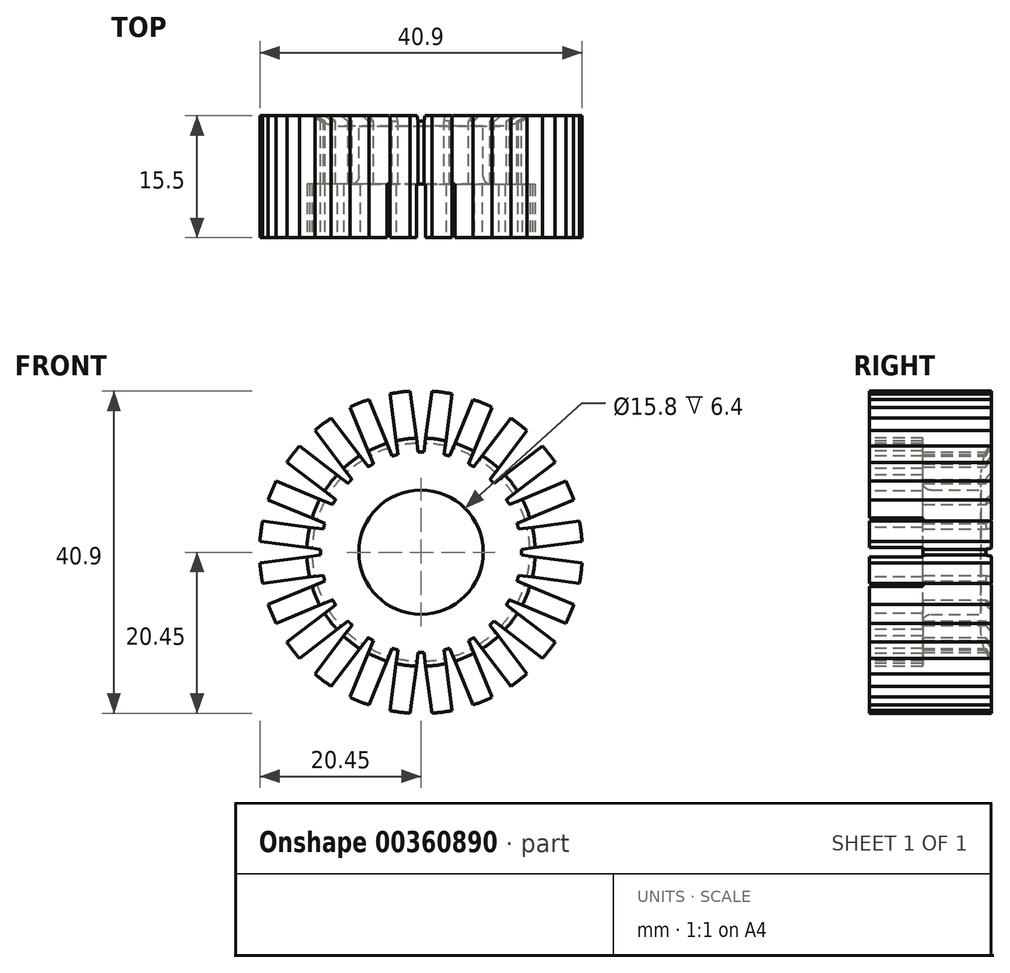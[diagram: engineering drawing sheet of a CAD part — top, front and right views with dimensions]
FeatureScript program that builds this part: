
annotation { "Feature Type Name" : "Feature", "Feature Type Description" : "" }
export const myFeature = defineFeature(function(context is Context, id is Id, definition is map)
    precondition{}
    {
        {
            var Q0;
            Q0=qCreatedBy(makeId("Front.planeOp"),FACE);
            var sketch = newSketch(context, id + "F0", { "sketchPlane" : qUnion([Q0])});
            skCircle(sketch, "E0", {"center": v(0, 0) * mm, "radius": 7.9 * mm});
            skCircle(sketch, "E1", {"center": v(0, 0) * mm, "radius": 12.75 * mm});
            skLineSegment(sketch, "E2", {"start": v(-29.1, 0) * mm, "end": v(30.08, 0) * mm, "construction": true});
            skLineSegment(sketch, "E3", {"start": v(4.61, 35.03) * mm, "end": v(-4.61, -35.03) * mm, "construction": true});
            skLineSegment(sketch, "E4", {"start": v(0.37, 12.74) * mm, "end": v(1.38, 20.45) * mm});
            skLineSegment(sketch, "E5", {"start": v(2.94, 12.4) * mm, "end": v(3.96, 20.11) * mm});
            skArc(sketch, "E6.trimOffspring", {"start": v(3.96, 20.11) * mm, "mid": v(2.68, 20.32) * mm, "end": v(1.38, 20.45) * mm});
            skLineSegment(sketch, "E7.1.0", {"start": v(6.05, 11.22) * mm, "end": v(9.03, 18.4) * mm});
            skArc(sketch, "E7.1.1", {"start": v(9.03, 18.4) * mm, "mid": v(7.85, 18.94) * mm, "end": v(6.63, 19.4) * mm});
            skLineSegment(sketch, "E7.1.2", {"start": v(3.65, 12.22) * mm, "end": v(6.63, 19.4) * mm});
            skLineSegment(sketch, "E7.2.0", {"start": v(8.75, 9.27) * mm, "end": v(13.49, 15.44) * mm});
            skArc(sketch, "E7.2.1", {"start": v(13.49, 15.44) * mm, "mid": v(12.48, 16.26) * mm, "end": v(11.42, 17.02) * mm});
            skLineSegment(sketch, "E7.2.2", {"start": v(6.69, 10.85) * mm, "end": v(11.42, 17.02) * mm});
            skLineSegment(sketch, "E7.3.0", {"start": v(10.85, 6.69) * mm, "end": v(17.02, 11.42) * mm});
            skArc(sketch, "E7.3.1", {"start": v(17.02, 11.42) * mm, "mid": v(16.26, 12.48) * mm, "end": v(15.44, 13.49) * mm});
            skLineSegment(sketch, "E7.3.2", {"start": v(9.27, 8.75) * mm, "end": v(15.44, 13.49) * mm});
            skLineSegment(sketch, "E7.4.0", {"start": v(12.22, 3.65) * mm, "end": v(19.4, 6.63) * mm});
            skArc(sketch, "E7.4.1", {"start": v(19.4, 6.63) * mm, "mid": v(18.94, 7.85) * mm, "end": v(18.4, 9.03) * mm});
            skLineSegment(sketch, "E7.4.2", {"start": v(11.22, 6.05) * mm, "end": v(18.4, 9.03) * mm});
            skLineSegment(sketch, "E7.5.0", {"start": v(12.74, 0.37) * mm, "end": v(20.45, 1.38) * mm});
            skArc(sketch, "E7.5.1", {"start": v(20.45, 1.38) * mm, "mid": v(20.32, 2.68) * mm, "end": v(20.11, 3.96) * mm});
            skLineSegment(sketch, "E7.5.2", {"start": v(12.4, 2.94) * mm, "end": v(20.11, 3.96) * mm});
            skLineSegment(sketch, "E7.6.0", {"start": v(12.4, -2.94) * mm, "end": v(20.11, -3.96) * mm});
            skArc(sketch, "E7.6.1", {"start": v(20.11, -3.96) * mm, "mid": v(20.32, -2.68) * mm, "end": v(20.45, -1.38) * mm});
            skLineSegment(sketch, "E7.6.2", {"start": v(12.74, -0.37) * mm, "end": v(20.45, -1.38) * mm});
            skLineSegment(sketch, "E7.7.0", {"start": v(11.22, -6.05) * mm, "end": v(18.4, -9.03) * mm});
            skArc(sketch, "E7.7.1", {"start": v(18.4, -9.03) * mm, "mid": v(18.94, -7.85) * mm, "end": v(19.4, -6.63) * mm});
            skLineSegment(sketch, "E7.7.2", {"start": v(12.22, -3.65) * mm, "end": v(19.4, -6.63) * mm});
            skLineSegment(sketch, "E7.anchor1", {"start": v(0, 0) * mm, "end": v(2.94, 12.4) * mm, "construction": true});
            skLineSegment(sketch, "E7.anchor2", {"start": v(0, 0) * mm, "end": v(-0.37, 12.74) * mm, "construction": true});
            skLineSegment(sketch, "E8.1.8.0", {"start": v(9.27, -8.75) * mm, "end": v(15.44, -13.49) * mm});
            skArc(sketch, "E8.3.8.0", {"start": v(15.44, -13.49) * mm, "mid": v(16.26, -12.48) * mm, "end": v(17.02, -11.42) * mm});
            skLineSegment(sketch, "E8.7.8.0", {"start": v(10.85, -6.69) * mm, "end": v(17.02, -11.42) * mm});
            skLineSegment(sketch, "E8.1.9.0", {"start": v(6.69, -10.85) * mm, "end": v(11.42, -17.02) * mm});
            skArc(sketch, "E8.3.9.0", {"start": v(11.42, -17.02) * mm, "mid": v(12.48, -16.26) * mm, "end": v(13.49, -15.44) * mm});
            skLineSegment(sketch, "E8.7.9.0", {"start": v(8.75, -9.27) * mm, "end": v(13.49, -15.44) * mm});
            skLineSegment(sketch, "E8.1.10.0", {"start": v(3.65, -12.22) * mm, "end": v(6.63, -19.4) * mm});
            skArc(sketch, "E8.3.10.0", {"start": v(6.63, -19.4) * mm, "mid": v(7.85, -18.94) * mm, "end": v(9.03, -18.4) * mm});
            skLineSegment(sketch, "E8.7.10.0", {"start": v(6.05, -11.22) * mm, "end": v(9.03, -18.4) * mm});
            skLineSegment(sketch, "E8.1.11.0", {"start": v(0.37, -12.74) * mm, "end": v(1.38, -20.45) * mm});
            skArc(sketch, "E8.3.11.0", {"start": v(1.38, -20.45) * mm, "mid": v(2.68, -20.32) * mm, "end": v(3.96, -20.11) * mm});
            skLineSegment(sketch, "E8.7.11.0", {"start": v(2.94, -12.4) * mm, "end": v(3.96, -20.11) * mm});
            skLineSegment(sketch, "E8.1.12.0", {"start": v(-2.94, -12.4) * mm, "end": v(-3.96, -20.11) * mm});
            skArc(sketch, "E8.3.12.0", {"start": v(-3.96, -20.11) * mm, "mid": v(-2.68, -20.32) * mm, "end": v(-1.38, -20.45) * mm});
            skLineSegment(sketch, "E8.7.12.0", {"start": v(-0.37, -12.74) * mm, "end": v(-1.38, -20.45) * mm});
            skLineSegment(sketch, "E8.1.13.0", {"start": v(-6.05, -11.22) * mm, "end": v(-9.03, -18.4) * mm});
            skArc(sketch, "E8.3.13.0", {"start": v(-9.03, -18.4) * mm, "mid": v(-7.85, -18.94) * mm, "end": v(-6.63, -19.4) * mm});
            skLineSegment(sketch, "E8.7.13.0", {"start": v(-3.65, -12.22) * mm, "end": v(-6.63, -19.4) * mm});
            skLineSegment(sketch, "E8.1.14.0", {"start": v(-8.75, -9.27) * mm, "end": v(-13.49, -15.44) * mm});
            skArc(sketch, "E8.3.14.0", {"start": v(-13.49, -15.44) * mm, "mid": v(-12.48, -16.26) * mm, "end": v(-11.42, -17.02) * mm});
            skLineSegment(sketch, "E8.7.14.0", {"start": v(-6.69, -10.85) * mm, "end": v(-11.42, -17.02) * mm});
            skLineSegment(sketch, "E8.1.15.0", {"start": v(-10.85, -6.69) * mm, "end": v(-17.02, -11.42) * mm});
            skArc(sketch, "E8.3.15.0", {"start": v(-17.02, -11.42) * mm, "mid": v(-16.26, -12.48) * mm, "end": v(-15.44, -13.49) * mm});
            skLineSegment(sketch, "E8.7.15.0", {"start": v(-9.27, -8.75) * mm, "end": v(-15.44, -13.49) * mm});
            skLineSegment(sketch, "E8.1.16.0", {"start": v(-12.22, -3.65) * mm, "end": v(-19.4, -6.63) * mm});
            skArc(sketch, "E8.3.16.0", {"start": v(-19.4, -6.63) * mm, "mid": v(-18.94, -7.85) * mm, "end": v(-18.4, -9.03) * mm});
            skLineSegment(sketch, "E8.7.16.0", {"start": v(-11.22, -6.05) * mm, "end": v(-18.4, -9.03) * mm});
            skLineSegment(sketch, "E8.1.17.0", {"start": v(-12.74, -0.37) * mm, "end": v(-20.45, -1.38) * mm});
            skArc(sketch, "E8.3.17.0", {"start": v(-20.45, -1.38) * mm, "mid": v(-20.32, -2.68) * mm, "end": v(-20.11, -3.96) * mm});
            skLineSegment(sketch, "E8.7.17.0", {"start": v(-12.4, -2.94) * mm, "end": v(-20.11, -3.96) * mm});
            skLineSegment(sketch, "E8.1.18.0", {"start": v(-12.4, 2.94) * mm, "end": v(-20.11, 3.96) * mm});
            skArc(sketch, "E8.3.18.0", {"start": v(-20.11, 3.96) * mm, "mid": v(-20.32, 2.68) * mm, "end": v(-20.45, 1.38) * mm});
            skLineSegment(sketch, "E8.7.18.0", {"start": v(-12.74, 0.37) * mm, "end": v(-20.45, 1.38) * mm});
            skLineSegment(sketch, "E8.1.19.0", {"start": v(-11.22, 6.05) * mm, "end": v(-18.4, 9.03) * mm});
            skArc(sketch, "E8.3.19.0", {"start": v(-18.4, 9.03) * mm, "mid": v(-18.94, 7.85) * mm, "end": v(-19.4, 6.63) * mm});
            skLineSegment(sketch, "E8.7.19.0", {"start": v(-12.22, 3.65) * mm, "end": v(-19.4, 6.63) * mm});
            skLineSegment(sketch, "E8.1.20.0", {"start": v(-9.27, 8.75) * mm, "end": v(-15.44, 13.49) * mm});
            skArc(sketch, "E8.3.20.0", {"start": v(-15.44, 13.49) * mm, "mid": v(-16.26, 12.48) * mm, "end": v(-17.02, 11.42) * mm});
            skLineSegment(sketch, "E8.7.20.0", {"start": v(-10.85, 6.69) * mm, "end": v(-17.02, 11.42) * mm});
            skLineSegment(sketch, "E8.1.21.0", {"start": v(-6.69, 10.85) * mm, "end": v(-11.42, 17.02) * mm});
            skArc(sketch, "E8.3.21.0", {"start": v(-11.42, 17.02) * mm, "mid": v(-12.48, 16.26) * mm, "end": v(-13.49, 15.44) * mm});
            skLineSegment(sketch, "E8.7.21.0", {"start": v(-8.75, 9.27) * mm, "end": v(-13.49, 15.44) * mm});
            skLineSegment(sketch, "E8.1.22.0", {"start": v(-3.65, 12.22) * mm, "end": v(-6.63, 19.4) * mm});
            skArc(sketch, "E8.3.22.0", {"start": v(-6.63, 19.4) * mm, "mid": v(-7.85, 18.94) * mm, "end": v(-9.03, 18.4) * mm});
            skLineSegment(sketch, "E8.7.22.0", {"start": v(-6.05, 11.22) * mm, "end": v(-9.03, 18.4) * mm});
            skLineSegment(sketch, "E8.1.23.0", {"start": v(-0.37, 12.74) * mm, "end": v(-1.38, 20.45) * mm});
            skArc(sketch, "E8.3.23.0", {"start": v(-1.38, 20.45) * mm, "mid": v(-2.68, 20.32) * mm, "end": v(-3.96, 20.11) * mm});
            skLineSegment(sketch, "E8.7.23.0", {"start": v(-2.94, 12.4) * mm, "end": v(-3.96, 20.11) * mm});
            skPoint(sketch, "E9", {"position": v(-16.26, 12.48) * mm});
            skPoint(sketch, "E10", {"position": v(16.26, -12.48) * mm});
            skSolve(sketch);
        }
        {
            var Q0;
            Q0=qSketchRegion(id+"F0",true);
            extrude(context, id + "F1", {"entities" : qUnion([Q0]), "depth" : 15.5 * mm});
        }
        {
            var Q0;
            Q0=makeQuery(id+"F1.opExtrude","CAP_FACE",FACE,{"disambiguationData":[OSD([sQuery(id+"F0.wireOp",EDGE,"E0"),sQuery(id+"F0.wireOp",EDGE,"E1"),sQuery(id+"F0.wireOp",EDGE,"E4"),sQuery(id+"F0.wireOp",EDGE,"E5"),sQuery(id+"F0.wireOp",EDGE,"E6.trimOffspring"),sQuery(id+"F0.wireOp",EDGE,"E7.1.0"),sQuery(id+"F0.wireOp",EDGE,"E7.1.1"),sQuery(id+"F0.wireOp",EDGE,"E7.1.2"),sQuery(id+"F0.wireOp",EDGE,"E7.2.0"),sQuery(id+"F0.wireOp",EDGE,"E7.2.1"),sQuery(id+"F0.wireOp",EDGE,"E7.2.2"),sQuery(id+"F0.wireOp",EDGE,"E7.3.0"),sQuery(id+"F0.wireOp",EDGE,"E7.3.1"),sQuery(id+"F0.wireOp",EDGE,"E7.3.2"),sQuery(id+"F0.wireOp",EDGE,"E7.4.0"),sQuery(id+"F0.wireOp",EDGE,"E7.4.1"),sQuery(id+"F0.wireOp",EDGE,"E7.4.2"),sQuery(id+"F0.wireOp",EDGE,"E7.5.0"),sQuery(id+"F0.wireOp",EDGE,"E7.5.1"),sQuery(id+"F0.wireOp",EDGE,"E7.5.2"),sQuery(id+"F0.wireOp",EDGE,"E7.6.0"),sQuery(id+"F0.wireOp",EDGE,"E7.6.1"),sQuery(id+"F0.wireOp",EDGE,"E7.6.2"),sQuery(id+"F0.wireOp",EDGE,"E7.7.0"),sQuery(id+"F0.wireOp",EDGE,"E7.7.1"),sQuery(id+"F0.wireOp",EDGE,"E7.7.2")])],"isStart":false});
            var sketch = newSketch(context, id + "F2", { "sketchPlane" : qUnion([Q0])});
            skCircle(sketch, "E11", {"center": v(0, 0) * mm, "radius": 12.75 * mm});
            skSolve(sketch);
        }
        {
            var Q0;
            Q0=qSketchRegion(id+"F2",true);
            extrude(context, id + "F3", {"entities" : qUnion([Q0]), "operationType" : NewBodyOperationType.REMOVE, "oppositeDirection" : true, "depth" : 6.8 * mm});
        }
        {
            var Q0;
            Q0=makeQuery(id+"F3.boolean.opBoolean","INTERSECT",EDGE,{"derivedFrom":[makeQuery(id+"F1.opExtrude","SWEPT_FACE",FACE,{"disambiguationData":[OSD([sQuery(id+"F0.wireOp",EDGE,"E0")])]}),makeQuery(id+"F3.opExtrude","CAP_FACE",FACE,{"disambiguationData":[OSD([sQuery(id+"F2.wireOp",EDGE,"E11")])],"isStart":false})]});
            fillet(context, id + "F4", {"entities" : qUnion([Q0]), "radius" : 1 * mm, "tangentPropagation" : true, "allowEdgeOverflow" : false});
        }
        {
            var Q0;
            Q0=qCreatedBy(makeId("Right.planeOp"),FACE);
            var sketch = newSketch(context, id + "F5", { "sketchPlane" : qUnion([Q0])});
            skLineSegment(sketch, "E12", {"start": v(0, 0) * mm, "end": v(0, -13.84) * mm});
            skLineSegment(sketch, "E13", {"start": v(-1.3, -10.1) * mm, "end": v(-1.3, 0) * mm});
            skLineSegment(sketch, "E14", {"start": v(0, 0) * mm, "end": v(-1.3, 0) * mm});
            skPoint(sketch, "E15.end.orphan", {"position": v(0, 13.84) * mm});
            skPoint(sketch, "E15.start.orphan", {"position": v(-1.3, 13.84) * mm});
            skArc(sketch, "E16", {"start": v(-1.3, -10.1) * mm, "mid": v(-0.97, -12.08) * mm, "end": v(0, -13.84) * mm});
            skPoint(sketch, "E17.end.orphan", {"position": v(-1.3, -13.84) * mm});
            skSolve(sketch);
        }
        {
            var Q0;
            Q0=qSketchRegion(id+"F5",true);
            var Q1;
            Q1=sQuery(id+"F5.wireOp",EDGE,"E14");
            revolve(context, id + "F6", {"operationType" : NewBodyOperationType.REMOVE, "entities" : qUnion([Q0]), "axis" : qUnion([Q1]), "revolveType" : RevolveType.FULL, "oppositeDirection" : true});
        }
        {
            var Q0;
            {var subQ0=sQuery(id+"F0.wireOp",EDGE,"E8.1.19.0");var subQ1=sQuery(id+"F0.wireOp",EDGE,"E8.3.19.0");var subQ2=sQuery(id+"F0.wireOp",EDGE,"E8.7.19.0");Q0=makeQuery(id+"F3.boolean.opBoolean","SPLIT",FACE,{"disambiguationData":[TD([makeQuery(id+"F1.opExtrude","SWEPT_FACE",FACE,{"disambiguationData":[OSD([subQ0])]})])],"derivedFrom":makeQuery(id+"F1.opExtrude","CAP_FACE",FACE,{"disambiguationData":[OSD([sQuery(id+"F0.wireOp",EDGE,"E0"),sQuery(id+"F0.wireOp",EDGE,"E1"),sQuery(id+"F0.wireOp",EDGE,"E4"),sQuery(id+"F0.wireOp",EDGE,"E5"),sQuery(id+"F0.wireOp",EDGE,"E6.trimOffspring"),sQuery(id+"F0.wireOp",EDGE,"E7.1.0"),sQuery(id+"F0.wireOp",EDGE,"E7.1.1"),sQuery(id+"F0.wireOp",EDGE,"E7.1.2"),sQuery(id+"F0.wireOp",EDGE,"E7.2.0"),sQuery(id+"F0.wireOp",EDGE,"E7.2.1"),sQuery(id+"F0.wireOp",EDGE,"E7.2.2"),sQuery(id+"F0.wireOp",EDGE,"E7.3.0"),sQuery(id+"F0.wireOp",EDGE,"E7.3.1"),sQuery(id+"F0.wireOp",EDGE,"E7.3.2"),sQuery(id+"F0.wireOp",EDGE,"E7.4.0"),sQuery(id+"F0.wireOp",EDGE,"E7.4.1"),sQuery(id+"F0.wireOp",EDGE,"E7.4.2"),sQuery(id+"F0.wireOp",EDGE,"E7.5.0"),sQuery(id+"F0.wireOp",EDGE,"E7.5.1"),sQuery(id+"F0.wireOp",EDGE,"E7.5.2"),sQuery(id+"F0.wireOp",EDGE,"E7.6.0"),sQuery(id+"F0.wireOp",EDGE,"E7.6.1"),sQuery(id+"F0.wireOp",EDGE,"E7.6.2"),sQuery(id+"F0.wireOp",EDGE,"E7.7.0"),sQuery(id+"F0.wireOp",EDGE,"E7.7.1"),sQuery(id+"F0.wireOp",EDGE,"E7.7.2"),sQuery(id+"F0.wireOp",EDGE,"E8.1.8.0"),sQuery(id+"F0.wireOp",EDGE,"E8.3.8.0"),sQuery(id+"F0.wireOp",EDGE,"E8.7.8.0"),sQuery(id+"F0.wireOp",EDGE,"E8.1.9.0"),sQuery(id+"F0.wireOp",EDGE,"E8.3.9.0"),sQuery(id+"F0.wireOp",EDGE,"E8.7.9.0"),sQuery(id+"F0.wireOp",EDGE,"E8.1.10.0"),sQuery(id+"F0.wireOp",EDGE,"E8.3.10.0"),sQuery(id+"F0.wireOp",EDGE,"E8.7.10.0"),sQuery(id+"F0.wireOp",EDGE,"E8.1.11.0"),sQuery(id+"F0.wireOp",EDGE,"E8.3.11.0"),sQuery(id+"F0.wireOp",EDGE,"E8.7.11.0"),sQuery(id+"F0.wireOp",EDGE,"E8.1.12.0"),sQuery(id+"F0.wireOp",EDGE,"E8.3.12.0"),sQuery(id+"F0.wireOp",EDGE,"E8.7.12.0"),sQuery(id+"F0.wireOp",EDGE,"E8.1.13.0"),sQuery(id+"F0.wireOp",EDGE,"E8.3.13.0"),sQuery(id+"F0.wireOp",EDGE,"E8.7.13.0"),sQuery(id+"F0.wireOp",EDGE,"E8.1.14.0"),sQuery(id+"F0.wireOp",EDGE,"E8.3.14.0"),sQuery(id+"F0.wireOp",EDGE,"E8.7.14.0"),sQuery(id+"F0.wireOp",EDGE,"E8.1.15.0"),sQuery(id+"F0.wireOp",EDGE,"E8.3.15.0"),sQuery(id+"F0.wireOp",EDGE,"E8.7.15.0"),sQuery(id+"F0.wireOp",EDGE,"E8.1.16.0"),sQuery(id+"F0.wireOp",EDGE,"E8.3.16.0"),sQuery(id+"F0.wireOp",EDGE,"E8.7.16.0"),sQuery(id+"F0.wireOp",EDGE,"E8.1.17.0"),sQuery(id+"F0.wireOp",EDGE,"E8.3.17.0"),sQuery(id+"F0.wireOp",EDGE,"E8.7.17.0"),sQuery(id+"F0.wireOp",EDGE,"E8.1.18.0"),sQuery(id+"F0.wireOp",EDGE,"E8.3.18.0"),sQuery(id+"F0.wireOp",EDGE,"E8.7.18.0"),subQ0,subQ1,subQ2,sQuery(id+"F0.wireOp",EDGE,"E8.1.20.0"),sQuery(id+"F0.wireOp",EDGE,"E8.3.20.0"),sQuery(id+"F0.wireOp",EDGE,"E8.7.20.0"),sQuery(id+"F0.wireOp",EDGE,"E8.1.21.0"),sQuery(id+"F0.wireOp",EDGE,"E8.3.21.0"),sQuery(id+"F0.wireOp",EDGE,"E8.7.21.0"),sQuery(id+"F0.wireOp",EDGE,"E8.1.22.0"),sQuery(id+"F0.wireOp",EDGE,"E8.3.22.0"),sQuery(id+"F0.wireOp",EDGE,"E8.7.22.0"),sQuery(id+"F0.wireOp",EDGE,"E8.1.23.0"),sQuery(id+"F0.wireOp",EDGE,"E8.3.23.0"),sQuery(id+"F0.wireOp",EDGE,"E8.7.23.0")])],"isStart":false})});}
            var sketch = newSketch(context, id + "F7", { "sketchPlane" : qUnion([Q0])});
            skLineSegment(sketch, "E18", {"start": v(0, 0) * mm, "end": v(-36.63, 0) * mm, "construction": true});
            skLineSegment(sketch, "E19", {"start": v(0, 0) * mm, "end": v(0, 29.2) * mm, "construction": true});
            skCircle(sketch, "E20", {"center": v(0, 0) * mm, "radius": 14.5 * mm});
            skSolve(sketch);
        }
        {
            var Q0;
            Q0 = qSketchRegion(id + "F7", true);
            var Q1;
            Q1=makeQuery(id+"F3.boolean.opBoolean","COPY",FACE,{"derivedFrom":makeQuery(id+"F3.opExtrude","CAP_FACE",FACE,{"disambiguationData":[OSD([sQuery(id+"F2.wireOp",EDGE,"E11")])],"isStart":false})});
            extrude(context, id + "F8", {"entities" : qUnion([Q0]), "operationType" : NewBodyOperationType.REMOVE, "endBound" : BoundingType.UP_TO_SURFACE, "oppositeDirection" : true, "endBoundEntityFace" : qUnion([Q1]), "depth" : 25 * mm});
        }
    });
